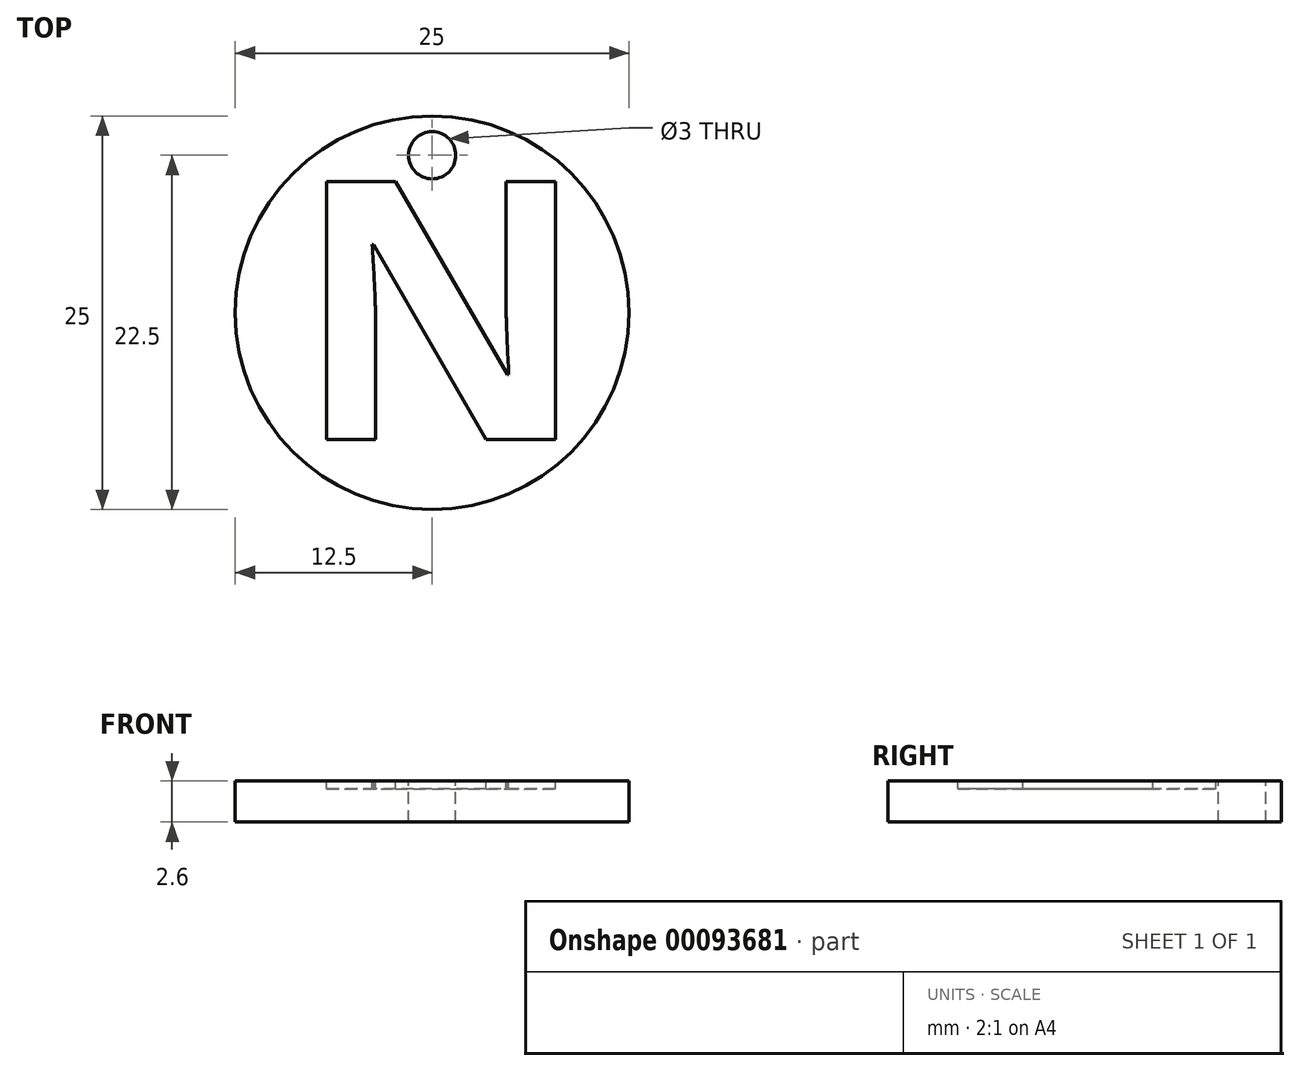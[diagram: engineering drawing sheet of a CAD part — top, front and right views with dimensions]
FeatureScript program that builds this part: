
annotation { "Feature Type Name" : "Feature", "Feature Type Description" : "" }
export const myFeature = defineFeature(function(context is Context, id is Id, definition is map)
    precondition{}
    {
        {
            var Q0;
            Q0=qCreatedBy(makeId("Top.planeOp"),FACE);
            var sketch = newSketch(context, id + "F0", { "sketchPlane" : qUnion([Q0])});
            skCircle(sketch, "E0", {"center": v(0, 0) * mm, "radius": 12.5 * mm});
            skSolve(sketch);
        }
        {
            var Q0;
            Q0=makeQuery(id+"F0.imprint","IMPRINT",FACE,{"disambiguationData":[TD([[makeQuery(id+"F0.imprint","IMPRINT",EDGE,{"derivedFrom":sQuery(id+"F0.wireOp",EDGE,"E0")}),1.0]])]});
            extrude(context, id + "F1", {"entities" : qUnion([Q0]), "depth" : 2.6 * mm});
        }
        {
            var Q0;
            Q0=makeQuery(id+"F1.opExtrude","CAP_FACE",FACE,{"disambiguationData":[OSD([sQuery(id+"F0.wireOp",EDGE,"E0")])],"isStart":false});
            var sketch = newSketch(context, id + "F2", { "sketchPlane" : qUnion([Q0])});
            skText(sketch, "E1", { "text": "N", "fontName": "OpenSans-Bold.ttf"});
            const initialGuessF2  = {"E1": [-0.00876, -0.00804, 1, 0, 0.01651]};
            skSetInitialGuess(sketch, initialGuessF2);
            skSolve(sketch);
        }
        {
            var Q0;
            Q0=makeQuery(id+"F2.imprint","IMPRINT",FACE,{"disambiguationData":[TD([[makeQuery(id+"F2.imprint","IMPRINT",EDGE,{"derivedFrom":sQuery(id+"F2.wireOp",EDGE,"E1.sketch_text.stroke-0")}),-1.0]])]});
            var Q1;
            Q1 = qConstructionFilter(qBodyType(qCreatedBy(id + "F2" ,EDGE), BodyType.WIRE), ConstructionObject.NO);
            extrude(context, id + "F3", {"entities" : qUnion([Q0]), "operationType" : NewBodyOperationType.REMOVE, "surfaceEntities" : qUnion([Q1]), "oppositeDirection" : true, "depth" : .5 * mm});
        }
        {
            var Q0;
            Q0=makeQuery(id+"F1.opExtrude","CAP_FACE",FACE,{"disambiguationData":[OSD([sQuery(id+"F0.wireOp",EDGE,"E0")])],"isStart":false});
            var sketch = newSketch(context, id + "F4", { "sketchPlane" : qUnion([Q0])});
            skCircle(sketch, "E2", {"center": v(0, 10) * mm, "radius": 1.5 * mm});
            skSolve(sketch);
        }
        {
            var Q0;
            Q0=makeQuery(id+"F4.imprint","IMPRINT",FACE,{"disambiguationData":[TD([[makeQuery(id+"F4.imprint","IMPRINT",EDGE,{"derivedFrom":sQuery(id+"F4.wireOp",EDGE,"E2")}),1.0]])]});
            extrude(context, id + "F5", {"entities" : qUnion([Q0]), "operationType" : NewBodyOperationType.REMOVE, "oppositeDirection" : true, "depth" : 25 * mm});
        }
    });
